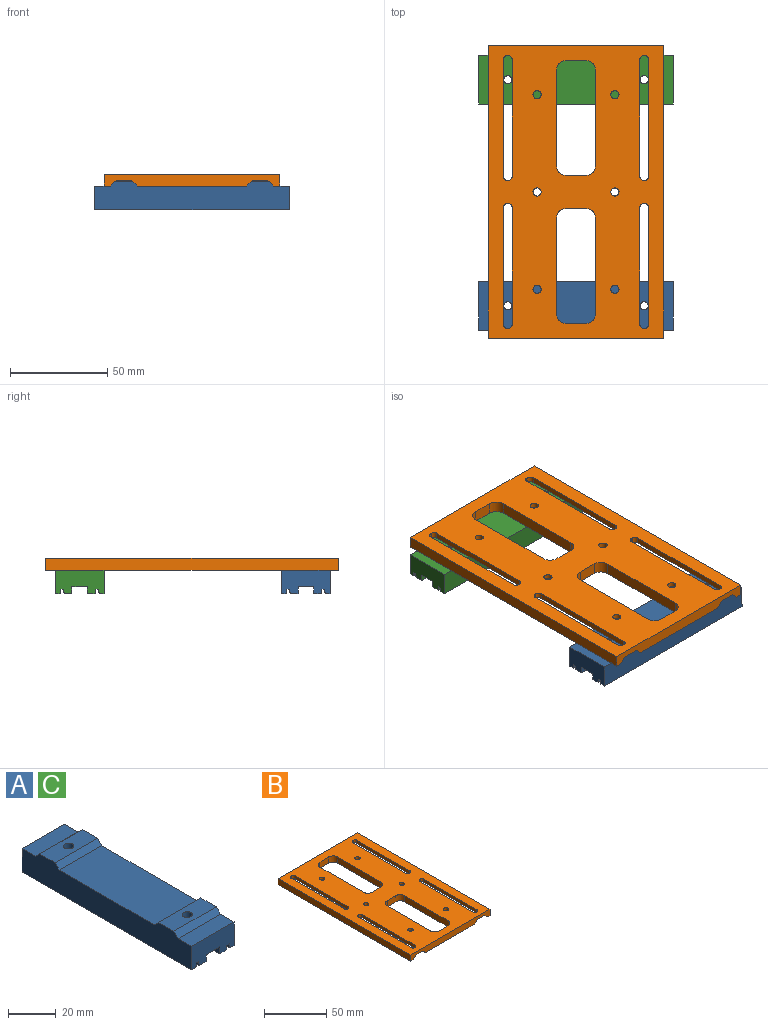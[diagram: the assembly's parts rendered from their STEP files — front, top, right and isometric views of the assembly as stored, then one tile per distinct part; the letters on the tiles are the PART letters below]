
ASSEMBLY  parts=3 mates=5
PART A: 50 faces, bbox 25x100x14.5 mm
  f0: plane 25x8mm, normal (0,0,1), area 200mm2, adj f10,f11,f13,f47
  f1: plane 56x25mm, normal (0,0,1), area 1400mm2, adj f11,f13,f45,f49
  f2: plane 100x8mm, normal (0,0,-1), area 710.2mm2, adj f9,f10,f14,f15,f30,f31,f32,f33
  f3: cylinder r=2.1mm len=7.8mm, axis (0,0,1), area 102.9mm2, adj f37,f48
  f4: cylinder r=2.1mm len=7.8mm, axis (0,0,1), area 102.9mm2, adj f36,f46
  f5: plane 25x8mm, normal (0,0,1), area 200mm2, adj f9,f11,f13,f44
  f6: plane 100x3.98mm, normal (0,0,-1), area 397.5mm2, adj f9,f10,f14,f23
  f7: plane 100x2.53mm, normal (0,0,-1), area 252.5mm2, adj f9,f10,f13,f16
  f8: plane 100x3.98mm, normal (0,0,-1), area 397.5mm2, adj f9,f10,f15,f22
  f9: plane 25x12mm, normal (0,-1,0), area 265.1mm2, adj f2,f5,f6,f7,f8,f11,f12,f13
  f10: plane 25x12mm, normal (0,1,0), area 265.1mm2, adj f0,f2,f6,f7,f8,f11,f12,f13
  f11: plane 100x14.5mm, normal (-1,0,0), area 1257.5mm2, adj f0,f1,f5,f9,f10,f12,f44,f45
  f12: plane 100x2.53mm, normal (0,0,-1), area 252.5mm2, adj f9,f10,f11,f27
  f13: plane 100x14.5mm, normal (1,0,0), area 1257.5mm2, adj f0,f1,f5,f7,f9,f10,f44,f45
  f14: plane 100x3.5mm, normal (1,0,0), area 350mm2, adj f2,f6,f9,f10
  f15: plane 100x3.5mm, normal (-1,0,0), area 350mm2, adj f2,f8,f9,f10
  f16: plane 100x0.3mm, normal (-1,0,0), area 30mm2, adj f7,f9,f10,f17
  f17: plane 100x0.25mm, normal (0,0,-1), area 25mm2, adj f9,f10,f16,f18
  f18: plane 100x1.9mm, normal (-1,0,0), area 190mm2, adj f9,f10,f17,f19
  f19: plane 100x1.5mm, normal (0,0,-1), area 150mm2, adj f9,f10,f18,f20
  f20: plane 100x1.9mm, normal (1,0,0), area 190mm2, adj f9,f10,f19,f21
  f21: plane 100x0.25mm, normal (0,0,-1), area 25mm2, adj f9,f10,f20,f22
  f22: plane 100x0.3mm, normal (1,0,0), area 30mm2, adj f8,f9,f10,f21
  f23: plane 100x0.3mm, normal (-1,0,0), area 30mm2, adj f6,f9,f10,f24
  f24: plane 100x0.25mm, normal (0,0,-1), area 25mm2, adj f9,f10,f23,f25
  f25: plane 100x1.9mm, normal (-1,0,0), area 190mm2, adj f9,f10,f24,f26
  f26: plane 100x1.5mm, normal (0,0,-1), area 150mm2, adj f9,f10,f25,f28
  f27: plane 100x0.3mm, normal (1,0,0), area 30mm2, adj f9,f10,f12,f29
  f28: plane 100x1.9mm, normal (1,0,0), area 190mm2, adj f9,f10,f26,f29
  f29: plane 100x0.25mm, normal (0,0,-1), area 25mm2, adj f9,f10,f27,f28
  f30: plane 3.6x3.2mm, normal (0.5,-0.87,0), area 13.3mm2, adj f2,f31,f35,f36
  f31: plane 3.6x3.2mm, normal (-0.5,-0.87,0), area 13.3mm2, adj f2,f30,f32,f36
  f32: plane 4.16x3.2mm, normal (-1,0,0), area 13.3mm2, adj f2,f31,f33,f36
  f33: plane 3.6x3.2mm, normal (-0.5,0.87,0), area 13.3mm2, adj f2,f32,f34,f36
  f34: plane 3.6x3.2mm, normal (0.5,0.87,0), area 13.3mm2, adj f2,f33,f35,f36
  f35: plane 4.16x3.2mm, normal (1,0,0), area 13.3mm2, adj f2,f30,f34,f36
  f36: plane 8.31x7.2mm, normal (0,0,-1), area 31mm2, adj f4,f30,f31,f32,f33,f34,f35
  f37: plane 8.31x7.2mm, normal (0,0,-1), area 31mm2, adj f3,f38,f39,f40,f41,f42,f43
  f38: plane 3.6x3.2mm, normal (0.5,-0.87,0), area 13.3mm2, adj f2,f37,f39,f43
  f39: plane 3.6x3.2mm, normal (-0.5,-0.87,0), area 13.3mm2, adj f2,f37,f38,f40
  f40: plane 4.16x3.2mm, normal (-1,0,0), area 13.3mm2, adj f2,f37,f39,f41
  f41: plane 3.6x3.2mm, normal (-0.5,0.87,0), area 13.3mm2, adj f2,f37,f40,f42
  f42: plane 3.6x3.2mm, normal (0.5,0.87,0), area 13.3mm2, adj f2,f37,f41,f43
  f43: plane 4.16x3.2mm, normal (1,0,0), area 13.3mm2, adj f2,f37,f38,f42
  f44: plane 25x2.5mm, normal (0,-0.71,0.71), area 88.4mm2, adj f5,f11,f13,f46
  f45: plane 25x2.5mm, normal (0,0.71,0.71), area 88.4mm2, adj f1,f11,f13,f46
  f46: plane 25x9mm, normal (0,0,1), area 211.1mm2, adj f4,f11,f13,f44,f45
  f47: plane 25x2.5mm, normal (0,0.71,0.71), area 88.4mm2, adj f0,f11,f13,f48
  f48: plane 25x9mm, normal (0,0,1), area 211.1mm2, adj f3,f11,f13,f47,f49
  f49: plane 25x2.5mm, normal (0,-0.71,0.71), area 88.4mm2, adj f1,f11,f13,f48
PART B: 110 faces, bbox 90x150x6 mm
  f0: plane 150x56mm, normal (0,0,-1), area 5813.6mm2, adj f10,f11,f15,f18,f53,f54,f55,f56
  f1: plane 150x90mm, normal (0,0,1), area 9961.5mm2, adj f2,f3,f4,f5,f6,f7,f10,f11
  f2: cylinder r=2.1mm len=4.2mm, axis (0,0,-1), area 33mm2, adj f1,f93
  f3: cylinder r=2.1mm len=4.2mm, axis (0,0,-1), area 33mm2, adj f1,f80
  f4: cylinder r=2.1mm len=4.2mm, axis (0,0,-1), area 33mm2, adj f1,f79
  f5: cylinder r=2.1mm len=4.2mm, axis (0,0,-1), area 33mm2, adj f1,f66
  f6: cylinder r=2.1mm len=4.2mm, axis (0,0,-1), area 33mm2, adj f1,f65
  f7: cylinder r=2.1mm len=4.2mm, axis (0,0,-1), area 33mm2, adj f1,f52
  f8: plane 150x8mm, normal (0,0,-1), area 630.9mm2, adj f10,f11,f15,f16,f36,f37,f38,f39
  f9: plane 150x3mm, normal (0,0,-1), area 450mm2, adj f10,f11,f14,f16
  f10: plane 90x6mm, normal (0,-1,0), area 474mm2, adj f0,f1,f8,f9,f12,f13,f14,f15
  f11: plane 90x6mm, normal (0,1,0), area 474mm2, adj f0,f1,f8,f9,f12,f13,f14,f15
  f12: plane 150x6mm, normal (-1,0,0), area 900mm2, adj f1,f10,f11,f13
  f13: plane 150x3mm, normal (0,0,-1), area 450mm2, adj f10,f11,f12,f17
  f14: plane 150x6mm, normal (1,0,0), area 900mm2, adj f1,f9,f10,f11
  f15: plane 150x3mm, normal (0.71,0,-0.71), area 636.4mm2, adj f0,f8,f10,f11
  f16: plane 150x3mm, normal (-0.71,0,-0.71), area 636.4mm2, adj f8,f9,f10,f11
  f17: plane 150x3mm, normal (0.71,0,-0.71), area 636.4mm2, adj f10,f11,f13,f19
  f18: plane 150x3mm, normal (-0.71,0,-0.71), area 636.4mm2, adj f0,f10,f11,f19
  f19: plane 150x8mm, normal (0,0,-1), area 630.9mm2, adj f10,f11,f17,f18,f20,f21,f22,f23
  f20: plane 60x3mm, normal (-1,0,0), area 180mm2, adj f1,f19,f21,f25
  f21: cylinder r=2mm len=3mm, axis (0,0,-1), area 9.4mm2, adj f1,f19,f20,f22
  f22: plane 3x0.5mm, normal (0,1,0), area 1.5mm2, adj f1,f19,f21,f23
  f23: cylinder r=2mm len=3mm, axis (0,0,-1), area 9.4mm2, adj f1,f19,f22,f24
  f24: plane 60x3mm, normal (1,0,0), area 180mm2, adj f1,f19,f23,f26
  f25: cylinder r=2mm len=3mm, axis (0,0,-1), area 9.4mm2, adj f1,f19,f20,f27
  f26: cylinder r=2mm len=3mm, axis (0,0,-1), area 9.4mm2, adj f1,f19,f24,f27
  f27: plane 3x0.5mm, normal (0,-1,0), area 1.5mm2, adj f1,f19,f25,f26
  f28: cylinder r=2mm len=3mm, axis (0,0,-1), area 9.4mm2, adj f1,f19,f29,f33
  f29: plane 3x0.5mm, normal (0,1,0), area 1.5mm2, adj f1,f19,f28,f30
  f30: cylinder r=2mm len=3mm, axis (0,0,-1), area 9.4mm2, adj f1,f19,f29,f31
  f31: plane 60x3mm, normal (1,0,0), area 180mm2, adj f1,f19,f30,f32
  f32: cylinder r=2mm len=3mm, axis (0,0,-1), area 9.4mm2, adj f1,f19,f31,f34
  f33: plane 60x3mm, normal (-1,0,0), area 180mm2, adj f1,f19,f28,f35
  f34: plane 3x0.5mm, normal (0,-1,0), area 1.5mm2, adj f1,f19,f32,f35
  f35: cylinder r=2mm len=3mm, axis (0,0,-1), area 9.4mm2, adj f1,f19,f33,f34
  f36: plane 60x3mm, normal (-1,0,0), area 180mm2, adj f1,f8,f37,f43
  f37: cylinder r=2mm len=3mm, axis (0,0,-1), area 9.4mm2, adj f1,f8,f36,f38
  f38: plane 3x0.5mm, normal (0,1,0), area 1.5mm2, adj f1,f8,f37,f39
  f39: cylinder r=2mm len=3mm, axis (0,0,-1), area 9.4mm2, adj f1,f8,f38,f40
  f40: plane 60x3mm, normal (1,0,0), area 180mm2, adj f1,f8,f39,f41
  f41: cylinder r=2mm len=3mm, axis (0,0,-1), area 9.4mm2, adj f1,f8,f40,f42
  f42: plane 3x0.5mm, normal (0,-1,0), area 1.5mm2, adj f1,f8,f41,f43
  f43: cylinder r=2mm len=3mm, axis (0,0,-1), area 9.4mm2, adj f1,f8,f36,f42
  f44: cylinder r=2mm len=3mm, axis (0,0,-1), area 9.4mm2, adj f1,f8,f45,f49
  f45: plane 60x3mm, normal (-1,0,0), area 180mm2, adj f1,f8,f44,f46
  f46: cylinder r=2mm len=3mm, axis (0,0,-1), area 9.4mm2, adj f1,f8,f45,f47
  f47: plane 3x0.5mm, normal (0,1,0), area 1.5mm2, adj f1,f8,f46,f48
  f48: cylinder r=2mm len=3mm, axis (0,0,-1), area 9.4mm2, adj f1,f8,f47,f50
  f49: plane 3x0.5mm, normal (0,-1,0), area 1.5mm2, adj f1,f8,f44,f51
  f50: plane 60x3mm, normal (1,0,0), area 180mm2, adj f1,f8,f48,f51
  f51: cylinder r=2mm len=3mm, axis (0,0,-1), area 9.4mm2, adj f1,f8,f49,f50
  f52: plane 8.31x7.2mm, normal (0,0,-1), area 31mm2, adj f7,f53,f54,f55,f56,f57,f58
  f53: plane 3.6x3.5mm, normal (0.5,-0.87,0), area 14.5mm2, adj f0,f52,f54,f58
  f54: plane 3.6x3.5mm, normal (-0.5,-0.87,0), area 14.5mm2, adj f0,f52,f53,f55
  f55: plane 4.16x3.5mm, normal (-1,0,0), area 14.5mm2, adj f0,f52,f54,f56
  f56: plane 3.6x3.5mm, normal (-0.5,0.87,0), area 14.5mm2, adj f0,f52,f55,f57
  f57: plane 3.6x3.5mm, normal (0.5,0.87,0), area 14.5mm2, adj f0,f52,f56,f58
  f58: plane 4.16x3.5mm, normal (1,0,0), area 14.5mm2, adj f0,f52,f53,f57
  f59: plane 4.16x3.5mm, normal (-1,0,0), area 14.5mm2, adj f0,f60,f64,f65
  f60: plane 3.6x3.5mm, normal (-0.5,0.87,0), area 14.5mm2, adj f0,f59,f61,f65
  f61: plane 3.6x3.5mm, normal (0.5,0.87,0), area 14.5mm2, adj f0,f60,f62,f65
  f62: plane 4.16x3.5mm, normal (1,0,0), area 14.5mm2, adj f0,f61,f63,f65
  f63: plane 3.6x3.5mm, normal (0.5,-0.87,0), area 14.5mm2, adj f0,f62,f64,f65
  f64: plane 3.6x3.5mm, normal (-0.5,-0.87,0), area 14.5mm2, adj f0,f59,f63,f65
  f65: plane 8.31x7.2mm, normal (0,0,-1), area 31mm2, adj f6,f59,f60,f61,f62,f63,f64
  f66: plane 8.31x7.2mm, normal (0,0,-1), area 31mm2, adj f5,f67,f68,f69,f70,f71,f72
  f67: plane 4.16x3.5mm, normal (-1,0,0), area 14.5mm2, adj f0,f66,f68,f72
  f68: plane 3.6x3.5mm, normal (-0.5,0.87,0), area 14.5mm2, adj f0,f66,f67,f69
  f69: plane 3.6x3.5mm, normal (0.5,0.87,0), area 14.5mm2, adj f0,f66,f68,f70
  f70: plane 4.16x3.5mm, normal (1,0,0), area 14.5mm2, adj f0,f66,f69,f71
  f71: plane 3.6x3.5mm, normal (0.5,-0.87,0), area 14.5mm2, adj f0,f66,f70,f72
  f72: plane 3.6x3.5mm, normal (-0.5,-0.87,0), area 14.5mm2, adj f0,f66,f67,f71
  f73: plane 3.6x3.5mm, normal (-0.5,-0.87,0), area 14.5mm2, adj f0,f74,f78,f79
  f74: plane 4.16x3.5mm, normal (-1,0,0), area 14.5mm2, adj f0,f73,f75,f79
  f75: plane 3.6x3.5mm, normal (-0.5,0.87,0), area 14.5mm2, adj f0,f74,f76,f79
  f76: plane 3.6x3.5mm, normal (0.5,0.87,0), area 14.5mm2, adj f0,f75,f77,f79
  f77: plane 4.16x3.5mm, normal (1,0,0), area 14.5mm2, adj f0,f76,f78,f79
  f78: plane 3.6x3.5mm, normal (0.5,-0.87,0), area 14.5mm2, adj f0,f73,f77,f79
  f79: plane 8.31x7.2mm, normal (0,0,-1), area 31mm2, adj f4,f73,f74,f75,f76,f77,f78
  f80: plane 8.31x7.2mm, normal (0,0,-1), area 31mm2, adj f3,f81,f82,f83,f84,f85,f86
  f81: plane 4.16x3.5mm, normal (1,0,0), area 14.5mm2, adj f0,f80,f82,f86
  f82: plane 3.6x3.5mm, normal (0.5,-0.87,0), area 14.5mm2, adj f0,f80,f81,f83
  f83: plane 3.6x3.5mm, normal (-0.5,-0.87,0), area 14.5mm2, adj f0,f80,f82,f84
  f84: plane 4.16x3.5mm, normal (-1,0,0), area 14.5mm2, adj f0,f80,f83,f85
  f85: plane 3.6x3.5mm, normal (-0.5,0.87,0), area 14.5mm2, adj f0,f80,f84,f86
  f86: plane 3.6x3.5mm, normal (0.5,0.87,0), area 14.5mm2, adj f0,f80,f81,f85
  f87: plane 4.16x3.5mm, normal (1,0,0), area 14.5mm2, adj f0,f88,f92,f93
  f88: plane 3.6x3.5mm, normal (0.5,-0.87,0), area 14.5mm2, adj f0,f87,f89,f93
  f89: plane 3.6x3.5mm, normal (-0.5,-0.87,0), area 14.5mm2, adj f0,f88,f90,f93
  f90: plane 4.16x3.5mm, normal (-1,0,0), area 14.5mm2, adj f0,f89,f91,f93
  f91: plane 3.6x3.5mm, normal (-0.5,0.87,0), area 14.5mm2, adj f0,f90,f92,f93
  f92: plane 3.6x3.5mm, normal (0.5,0.87,0), area 14.5mm2, adj f0,f87,f91,f93
  f93: plane 8.31x7.2mm, normal (0,0,-1), area 31mm2, adj f2,f87,f88,f89,f90,f91,f92
  f94: cylinder r=5mm len=6mm, axis (0,0,1), area 47.1mm2, adj f0,f1,f95,f101
  f95: plane 49x6mm, normal (-1,0,0), area 294mm2, adj f0,f1,f94,f96
  f96: cylinder r=5mm len=6mm, axis (0,0,1), area 47.1mm2, adj f0,f1,f95,f97
  f97: plane 10x6mm, normal (0,-1,0), area 60mm2, adj f0,f1,f96,f98
  f98: cylinder r=5mm len=6mm, axis (0,0,1), area 47.1mm2, adj f0,f1,f97,f99
  f99: plane 49x6mm, normal (1,0,0), area 294mm2, adj f0,f1,f98,f100
  f100: cylinder r=5mm len=6mm, axis (0,0,1), area 47.1mm2, adj f0,f1,f99,f101
  f101: plane 10x6mm, normal (0,1,0), area 60mm2, adj f0,f1,f94,f100
  f102: plane 49x6mm, normal (-1,0,0), area 294mm2, adj f0,f1,f103,f109
  f103: cylinder r=5mm len=6mm, axis (0,0,1), area 47.1mm2, adj f0,f1,f102,f104
  f104: plane 10x6mm, normal (0,-1,0), area 60mm2, adj f0,f1,f103,f105
  f105: cylinder r=5mm len=6mm, axis (0,0,1), area 47.1mm2, adj f0,f1,f104,f106
  f106: plane 49x6mm, normal (1,0,0), area 294mm2, adj f0,f1,f105,f107
  f107: cylinder r=5mm len=6mm, axis (0,0,1), area 47.1mm2, adj f0,f1,f106,f108
  f108: plane 10x6mm, normal (0,1,0), area 60mm2, adj f0,f1,f107,f109
  f109: cylinder r=5mm len=6mm, axis (0,0,1), area 47.1mm2, adj f0,f1,f102,f108
PART C: same geometry as A
PLACE A rot(axis=(0,0,-1),90deg) t=(1.35,-59.32,-11.44)mm
PLACE B t=(1.35,-0.85,0.56)mm fixed
PLACE C rot(axis=(0,0,-1),90deg) t=(1.35,56.85,-11.44)mm
MATE planar A.f10 <-> C.f10  axis (1,0,0) through (51.35,-46.82,-5.44)mm
MATE planar C.f47 <-> B.f16  axis (0.71,0,0.71) through (42.1,56.85,1.81)mm
MATE parallel C.f13 <-> B.f10  axis (0,-1,0) through (-27.9,44.35,1.81)mm
MATE planar B.f0 <-> A.f0  axis (0,0,-1) through (1.35,74.15,0.56)mm
MATE planar A.f8 <-> C.f8  axis (0,0,-1) through (51.35,-65.31,-11.44)mm
